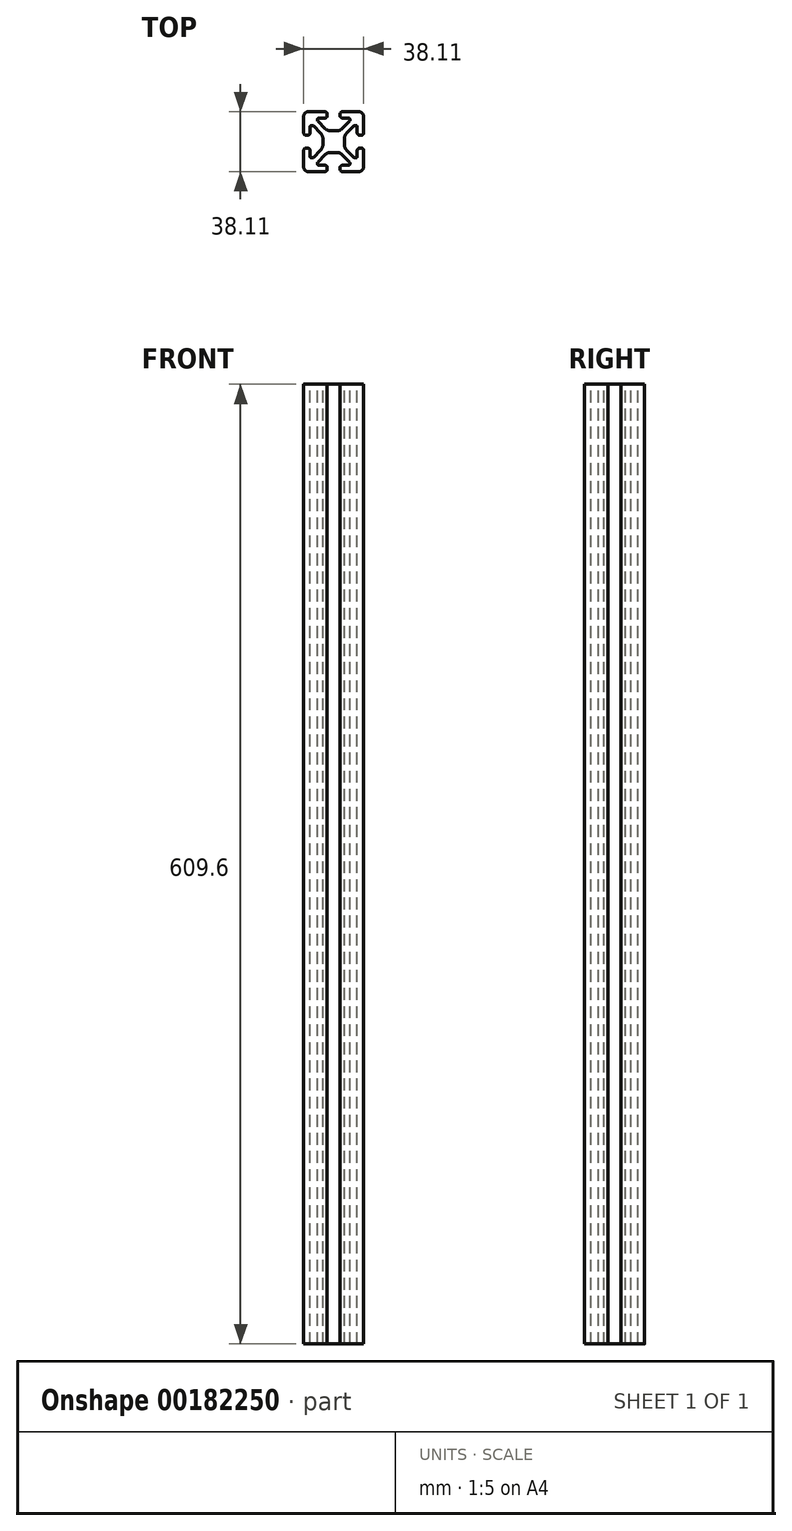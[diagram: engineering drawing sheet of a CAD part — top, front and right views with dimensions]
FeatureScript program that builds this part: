
annotation { "Feature Type Name" : "Feature", "Feature Type Description" : "" }
export const myFeature = defineFeature(function(context is Context, id is Id, definition is map)
    precondition{}
    {
        {
            var Q0;
            Q0=qCreatedBy(makeId("Top.planeOp"),FACE);
            var sketch = newSketch(context, id + "F0", { "sketchPlane" : qUnion([Q0])});
            skLineSegment(sketch, "E0.0", {"start": v(-3.18, 31.75) * mm, "end": v(-3.18, 21.51) * mm});
            skArc(sketch, "E1.0", {"start": v(0, 34.93) * mm, "mid": v(-2.25, 34) * mm, "end": v(-3.18, 31.75) * mm});
            skArc(sketch, "E2.0", {"start": v(-3.18, 21.51) * mm, "mid": v(-2.71, 20.4) * mm, "end": v(-1.6, 19.94) * mm});
            skLineSegment(sketch, "E3.0", {"start": v(-1.6, 19.94) * mm, "end": v(-0.69, 19.94) * mm});
            skArc(sketch, "E4.0", {"start": v(-0.69, 19.94) * mm, "mid": v(0.43, 20.4) * mm, "end": v(0.89, 21.51) * mm});
            skLineSegment(sketch, "E5.0", {"start": v(0.89, 21.51) * mm, "end": v(0.89, 25.27) * mm});
            skArc(sketch, "E6.0", {"start": v(0.89, 25.27) * mm, "mid": v(1.15, 25.9) * mm, "end": v(1.78, 26.16) * mm});
            skLineSegment(sketch, "E7.0", {"start": v(1.78, 26.16) * mm, "end": v(2.35, 26.16) * mm});
            skArc(sketch, "E8.0", {"start": v(2.35, 26.16) * mm, "mid": v(2.69, 26.1) * mm, "end": v(2.97, 25.9) * mm});
            skLineSegment(sketch, "E9.0", {"start": v(2.97, 25.9) * mm, "end": v(7.61, 21.26) * mm});
            skArc(sketch, "E10.0", {"start": v(7.61, 21.26) * mm, "mid": v(8.64, 19.72) * mm, "end": v(9, 17.9) * mm});
            skLineSegment(sketch, "E11.0", {"start": v(9, 17.9) * mm, "end": v(9, 13.85) * mm});
            skArc(sketch, "E12.0", {"start": v(9, 13.85) * mm, "mid": v(8.64, 12.03) * mm, "end": v(7.61, 10.49) * mm});
            skLineSegment(sketch, "E13.0", {"start": v(7.61, 10.49) * mm, "end": v(2.97, 5.85) * mm});
            skArc(sketch, "E14.0", {"start": v(2.97, 5.85) * mm, "mid": v(2.69, 5.66) * mm, "end": v(2.35, 5.59) * mm});
            skLineSegment(sketch, "E15.0", {"start": v(2.35, 5.59) * mm, "end": v(1.78, 5.59) * mm});
            skArc(sketch, "E16.0", {"start": v(1.78, 5.59) * mm, "mid": v(1.15, 5.85) * mm, "end": v(0.89, 6.48) * mm});
            skLineSegment(sketch, "E17.0", {"start": v(0.89, 6.48) * mm, "end": v(0.89, 10.24) * mm});
            skArc(sketch, "E18.0", {"start": v(0.89, 10.24) * mm, "mid": v(0.43, 11.35) * mm, "end": v(-0.69, 11.81) * mm});
            skLineSegment(sketch, "E19.0", {"start": v(-0.69, 11.81) * mm, "end": v(-1.6, 11.81) * mm});
            skArc(sketch, "E20.0", {"start": v(-1.6, 11.81) * mm, "mid": v(-2.71, 11.35) * mm, "end": v(-3.17, 10.24) * mm});
            skLineSegment(sketch, "E21.0", {"start": v(-3.17, 10.24) * mm, "end": v(-3.17, 0) * mm});
            skArc(sketch, "E22.0", {"start": v(-3.17, 0) * mm, "mid": v(-2.25, -2.25) * mm, "end": v(0, -3.17) * mm});
            skLineSegment(sketch, "E23.0", {"start": v(0, -3.17) * mm, "end": v(10.24, -3.17) * mm});
            skArc(sketch, "E24.0", {"start": v(10.24, -3.17) * mm, "mid": v(11.35, -2.71) * mm, "end": v(11.81, -1.6) * mm});
            skLineSegment(sketch, "E25.0", {"start": v(11.81, -1.6) * mm, "end": v(11.81, -0.69) * mm});
            skArc(sketch, "E26.0", {"start": v(11.81, -0.69) * mm, "mid": v(11.35, 0.43) * mm, "end": v(10.24, 0.89) * mm});
            skLineSegment(sketch, "E27.0", {"start": v(10.24, 0.89) * mm, "end": v(6.48, 0.89) * mm});
            skArc(sketch, "E28.0", {"start": v(6.48, 0.89) * mm, "mid": v(5.85, 1.15) * mm, "end": v(5.59, 1.78) * mm});
            skLineSegment(sketch, "E29.0", {"start": v(5.59, 1.78) * mm, "end": v(5.59, 2.35) * mm});
            skArc(sketch, "E30.0", {"start": v(5.59, 2.35) * mm, "mid": v(5.66, 2.69) * mm, "end": v(5.85, 2.97) * mm});
            skLineSegment(sketch, "E31.0", {"start": v(5.85, 2.97) * mm, "end": v(10.49, 7.61) * mm});
            skArc(sketch, "E32.0", {"start": v(10.49, 7.61) * mm, "mid": v(12.03, 8.64) * mm, "end": v(13.85, 9) * mm});
            skLineSegment(sketch, "E33.0", {"start": v(13.85, 9) * mm, "end": v(17.9, 9) * mm});
            skArc(sketch, "E34.0", {"start": v(17.9, 9) * mm, "mid": v(19.72, 8.64) * mm, "end": v(21.26, 7.61) * mm});
            skLineSegment(sketch, "E35.0", {"start": v(21.26, 7.61) * mm, "end": v(25.9, 2.97) * mm});
            skArc(sketch, "E36.0", {"start": v(25.9, 2.97) * mm, "mid": v(26.1, 2.69) * mm, "end": v(26.16, 2.35) * mm});
            skPoint(sketch, "E37.0", {"position": v(26.16, 1.78) * mm});
            skArc(sketch, "E38.0", {"start": v(26.16, 1.78) * mm, "mid": v(25.9, 1.15) * mm, "end": v(25.27, 0.89) * mm});
            skLineSegment(sketch, "E39.0", {"start": v(25.27, 0.89) * mm, "end": v(21.51, 0.89) * mm});
            skArc(sketch, "E40.0", {"start": v(21.51, 0.89) * mm, "mid": v(20.4, 0.43) * mm, "end": v(19.94, -0.69) * mm});
            skPoint(sketch, "E41.0", {"position": v(19.94, -1.6) * mm});
            skLineSegment(sketch, "E42.0", {"start": v(19.94, -0.69) * mm, "end": v(19.94, -1.6) * mm});
            skArc(sketch, "E43.0", {"start": v(19.94, -1.6) * mm, "mid": v(20.4, -2.71) * mm, "end": v(21.51, -3.17) * mm});
            skLineSegment(sketch, "E44.0", {"start": v(21.51, -3.17) * mm, "end": v(31.75, -3.17) * mm});
            skArc(sketch, "E45.0", {"start": v(31.75, -3.17) * mm, "mid": v(34, -2.25) * mm, "end": v(34.93, 0) * mm});
            skLineSegment(sketch, "E46.0", {"start": v(34.93, 0) * mm, "end": v(34.93, 10.24) * mm});
            skArc(sketch, "E47.0", {"start": v(34.93, 10.24) * mm, "mid": v(34.46, 11.35) * mm, "end": v(33.35, 11.81) * mm});
            skLineSegment(sketch, "E48.0", {"start": v(33.35, 11.81) * mm, "end": v(32.44, 11.81) * mm});
            skArc(sketch, "E49.0", {"start": v(32.44, 11.81) * mm, "mid": v(31.32, 11.35) * mm, "end": v(30.86, 10.24) * mm});
            skLineSegment(sketch, "E50.0", {"start": v(30.86, 10.24) * mm, "end": v(30.86, 6.48) * mm});
            skArc(sketch, "E51.0", {"start": v(30.86, 6.48) * mm, "mid": v(30.6, 5.85) * mm, "end": v(29.97, 5.59) * mm});
            skLineSegment(sketch, "E52.0", {"start": v(29.97, 5.59) * mm, "end": v(29.4, 5.59) * mm});
            skArc(sketch, "E53.0", {"start": v(29.4, 5.59) * mm, "mid": v(29.06, 5.66) * mm, "end": v(28.78, 5.85) * mm});
            skLineSegment(sketch, "E54.0", {"start": v(28.78, 5.85) * mm, "end": v(24.14, 10.49) * mm});
            skArc(sketch, "E55.0", {"start": v(24.14, 10.49) * mm, "mid": v(23.1, 12.03) * mm, "end": v(22.74, 13.85) * mm});
            skLineSegment(sketch, "E56.0", {"start": v(22.74, 13.85) * mm, "end": v(22.74, 17.9) * mm});
            skArc(sketch, "E57.0", {"start": v(22.74, 17.9) * mm, "mid": v(23.1, 19.72) * mm, "end": v(24.14, 21.26) * mm});
            skLineSegment(sketch, "E58.0", {"start": v(24.14, 21.26) * mm, "end": v(28.78, 25.9) * mm});
            skArc(sketch, "E59.0", {"start": v(28.78, 25.9) * mm, "mid": v(29.06, 26.1) * mm, "end": v(29.4, 26.16) * mm});
            skLineSegment(sketch, "E60.0", {"start": v(29.4, 26.16) * mm, "end": v(29.97, 26.16) * mm});
            skArc(sketch, "E61.0", {"start": v(29.97, 26.16) * mm, "mid": v(30.6, 25.9) * mm, "end": v(30.86, 25.27) * mm});
            skLineSegment(sketch, "E62.0", {"start": v(30.86, 25.27) * mm, "end": v(30.86, 21.51) * mm});
            skArc(sketch, "E63.0", {"start": v(30.86, 21.51) * mm, "mid": v(31.32, 20.4) * mm, "end": v(32.44, 19.94) * mm});
            skLineSegment(sketch, "E64.0", {"start": v(32.44, 19.94) * mm, "end": v(33.35, 19.94) * mm});
            skArc(sketch, "E65.0", {"start": v(33.35, 19.94) * mm, "mid": v(34.46, 20.4) * mm, "end": v(34.93, 21.51) * mm});
            skLineSegment(sketch, "E66.0", {"start": v(34.93, 21.51) * mm, "end": v(34.93, 31.75) * mm});
            skArc(sketch, "E67.0", {"start": v(34.93, 31.75) * mm, "mid": v(34, 34) * mm, "end": v(31.75, 34.93) * mm});
            skLineSegment(sketch, "E68.0", {"start": v(31.75, 34.93) * mm, "end": v(21.51, 34.93) * mm});
            skArc(sketch, "E69.0", {"start": v(21.51, 34.93) * mm, "mid": v(20.4, 34.46) * mm, "end": v(19.94, 33.35) * mm});
            skLineSegment(sketch, "E70.0", {"start": v(19.94, 33.35) * mm, "end": v(19.94, 32.44) * mm});
            skArc(sketch, "E71.0", {"start": v(19.94, 32.44) * mm, "mid": v(20.4, 31.32) * mm, "end": v(21.51, 30.86) * mm});
            skLineSegment(sketch, "E72.0", {"start": v(21.51, 30.86) * mm, "end": v(25.27, 30.86) * mm});
            skArc(sketch, "E73.0", {"start": v(25.27, 30.86) * mm, "mid": v(25.9, 30.6) * mm, "end": v(26.16, 29.97) * mm});
            skLineSegment(sketch, "E74.0", {"start": v(26.16, 29.97) * mm, "end": v(26.16, 29.4) * mm});
            skArc(sketch, "E75.0", {"start": v(26.16, 29.4) * mm, "mid": v(26.1, 29.06) * mm, "end": v(25.9, 28.78) * mm});
            skLineSegment(sketch, "E76.0", {"start": v(25.9, 28.78) * mm, "end": v(21.26, 24.14) * mm});
            skArc(sketch, "E77.0", {"start": v(11.81, 33.35) * mm, "mid": v(11.35, 34.46) * mm, "end": v(10.24, 34.93) * mm});
            skLineSegment(sketch, "E78.0", {"start": v(11.81, 32.44) * mm, "end": v(11.81, 33.35) * mm});
            skArc(sketch, "E79.0", {"start": v(10.24, 30.86) * mm, "mid": v(11.35, 31.32) * mm, "end": v(11.81, 32.44) * mm});
            skLineSegment(sketch, "E80.0", {"start": v(6.48, 30.86) * mm, "end": v(10.24, 30.86) * mm});
            skArc(sketch, "E81.0", {"start": v(5.59, 29.97) * mm, "mid": v(5.85, 30.6) * mm, "end": v(6.48, 30.86) * mm});
            skLineSegment(sketch, "E82.0", {"start": v(5.59, 29.4) * mm, "end": v(5.59, 29.97) * mm});
            skArc(sketch, "E83.0", {"start": v(5.85, 28.78) * mm, "mid": v(5.66, 29.06) * mm, "end": v(5.59, 29.4) * mm});
            skLineSegment(sketch, "E84.0", {"start": v(10.49, 24.14) * mm, "end": v(5.85, 28.78) * mm});
            skArc(sketch, "E85.0", {"start": v(13.85, 22.74) * mm, "mid": v(12.03, 23.1) * mm, "end": v(10.49, 24.14) * mm});
            skLineSegment(sketch, "E86.0", {"start": v(17.9, 22.74) * mm, "end": v(13.85, 22.74) * mm});
            skArc(sketch, "E87.0", {"start": v(21.26, 24.14) * mm, "mid": v(19.72, 23.1) * mm, "end": v(17.9, 22.74) * mm});
            skLineSegment(sketch, "E88.0", {"start": v(26.16, 2.35) * mm, "end": v(26.16, 1.78) * mm});
            skLineSegment(sketch, "E89", {"start": v(0, 34.93) * mm, "end": v(10.24, 34.93) * mm});
            skSolve(sketch);
        }
        {
            var Q0;
            Q0=qSketchRegion(id+"F0",true);
            extrude(context, id + "F1", {"entities" : qUnion([Q0]), "oppositeDirection" : true, "depth" : 609.6 * mm});
        }
    });
